# Revit family: Drinking_Fountain-Haws_Corporation-Wall_Mounted_1011.8
name_source: partatom
category: Plumbing Fixtures
revit_build: Autodesk Revit 2018 (Build: 20170223_1515(x64)
units: mm (PartAtom-declared; Revit-internal decimal feet)

## family parameters
Always vertical = Yes
Cut with Voids When Loaded = No
Host = Wall
OmniClass Number = 23.65.70.14.11
OmniClass Title = Drinking Fountains/Coolers
Part Type = Normal
Room Calculation Point = No
Round Connector Dimension = Use Radius
Shared = Yes

## types (3) — shared parameters
Apparent Load = 575 VA
Assembly Code = D2010810
BIMobject category = Taps & Mixers
BIMobject category code = sanitary-taps-mixers
BIMobject main category = Sanitary
BIMobject main category code = sanitary
Back Panel = Metal - Haws Corporation - Satin Stainless Steel
Bowl = Metal - Haws Corporation - Satin Stainless Steel
Bowl Diameter = 14 1/8"
Bracket = Metal - Haws Corporation - Satin Stainless Steel
Brand url = https://www.hawsco.com
CW Connection = Yes
CWFU = 2
Cost = $0
Cost Note = For Cost information please visit the Resource tab in the Product Page URL
Current = 5 A
Date of publishing = 3/24/2014
Description = "Hi-Lo" electric drinking fountain provides 8 gph chilled water performance
Design country = United States
Edition number = 1
Electrical Connection Note = Electrical connection is only required for products that contain touchless sensors
HW Connection = No
Keynote = 15410.A1
LEED = http://www.hawsco.com
Manufacturer = Haws Corporation 1455 Kleppe Lane Sparks, NV 89431
Manufacturer country = United States
Manufacturer name = Haws Corporation
MasterFormat 2004 = 22 47 00,22 47 13,22 52 00,22 52 13
Masterformat 2014 Code = 22 47 13
Masterformat 2014 Description = Drinking Fountains
Material main = Metal
Nominal height = 39"
Nominal width = 32"
Number of Poles = 1
OmniClass 23 = 23-65 70 14,23-65 70 14 11,23-65 70 14 11 11
OmniClass Code = 23-31 31 00
OmniClass Description = Drinking Fountains
Power Factor = 1
Product Page URL = https://www.hawsco.com
Product SKU = haws-h1011_8
Product certification = http://www.csagroup.org
Product family = Drinking Fountains/Coolers
Product group = Wall Mounted Drinking Fountains
Revisions Date = 05/24/2009
Sanitary Radius = 5/8"
Series = The Haws 1011 barrier free Hi-Lo drinking fountain
Supply Radius = 3/16"
Trim = Metal - Haws Corporation - Satin Stainless Steel
Trim Plate = Yes
Tubing = Metal - Haws Corporation - Copper
Tubing pos.R = 3 15/16"
Type Comments = Designed to run at a low energy usage, this water cooler and fountain are assured to have a long lasting life.
URL = http://www.hawsco.com
Uniclass 1.4 Code = L7213
Uniclass 1.4 Description = Fountains
Uniclass 2.0 Code = SS-35-65-70-25
Uniclass 2.0 Description = Drinking Fountain Systems
Uniclass 2015 Code = Pr_40_20_87_24
Uniclass 2015 Name = Drinking fountains
Vent Connection = Yes
Voltage = 115 V
WFU = 3
Waste Connection = No
Waste Level = 28 3/32"
Weight Net (Kg) = 56
zero-valued in all types: HWFU

## per-type parameters (varying)
| type | Nr | Nr 2 | Product data url | QR code | Sensor 1 | Sensor 2 |
| H1011.8 | 2 | 2 | https://bimobject.com | http://bimobject.com | No | No |
| H1011.8HO | 3 | 2 | https://www.bimobject.com | https://www.bimobject.com | Yes | No |
| H1011.8HO2 | 3 | 3 | https://www.bimobject.com | https://www.bimobject.com | Yes | Yes |

note: column(s) folded — value = type name in every type: Model

## geometry (parser evidence)
native form markers: Blend x24, Sweep x15
no freeform markers — native parametric forms only
